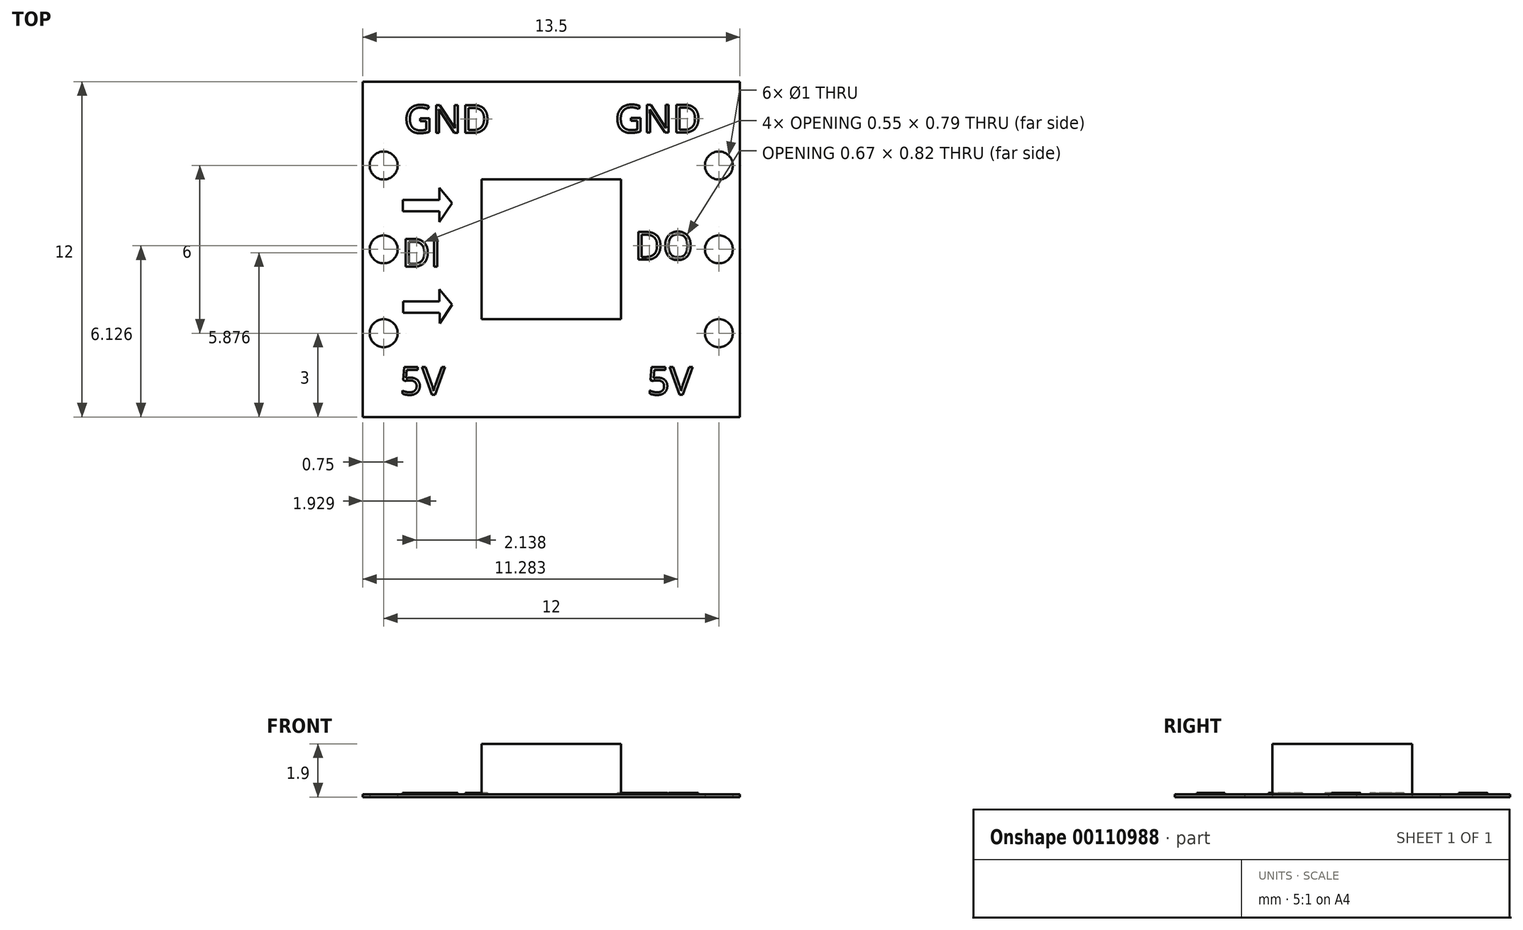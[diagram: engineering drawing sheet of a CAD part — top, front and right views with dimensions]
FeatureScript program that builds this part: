
annotation { "Feature Type Name" : "Feature", "Feature Type Description" : "" }
export const myFeature = defineFeature(function(context is Context, id is Id, definition is map)
    precondition{}
    {
        {
            var Q0;
            Q0=qCreatedBy(makeId("Top.planeOp"),FACE);
            var sketch = newSketch(context, id + "F0", { "sketchPlane" : qUnion([Q0])});
            skLineSegment(sketch, "E0.bottom", {"start": v(6.75, 6) * mm, "end": v(-6.75, 6) * mm});
            skLineSegment(sketch, "E0.top", {"start": v(6.75, -6) * mm, "end": v(-6.75, -6) * mm});
            skLineSegment(sketch, "E0.left", {"start": v(6.75, 6) * mm, "end": v(6.75, -6) * mm});
            skLineSegment(sketch, "E0.right", {"start": v(-6.75, 6) * mm, "end": v(-6.75, -6) * mm});
            skPoint(sketch, "E0.middle", {"position": v(0, 0) * mm});
            skCircle(sketch, "E1", {"center": v(-6, 3) * mm, "radius": 0.5 * mm});
            skCircle(sketch, "E2", {"center": v(6, 3) * mm, "radius": 0.5 * mm});
            skCircle(sketch, "E3.1.0.0", {"center": v(-6, 0) * mm, "radius": 0.5 * mm});
            skCircle(sketch, "E3.1.0.1", {"center": v(6, 0) * mm, "radius": 0.5 * mm});
            skCircle(sketch, "E3.2.0.0", {"center": v(-6, -3) * mm, "radius": 0.5 * mm});
            skCircle(sketch, "E3.2.0.1", {"center": v(6, -3) * mm, "radius": 0.5 * mm});
            skLineSegment(sketch, "E3.direction1", {"start": v(-6, 3) * mm, "end": v(-6, 0) * mm, "construction": true});
            skSolve(sketch);
        }
        {
            var Q0;
            Q0 = qSketchRegion(id + "F0", true);
            extrude(context, id + "F1", {"entities" : qUnion([Q0]), "depth" : 0.1 * mm});
        }
        {
            var Q0;
            Q0=makeQuery(id+"F1.opExtrude","CAP_FACE",FACE,{"disambiguationData":[OSD([sQuery(id+"F0.wireOp",EDGE,"E0.bottom"),sQuery(id+"F0.wireOp",EDGE,"E0.top"),sQuery(id+"F0.wireOp",EDGE,"E0.left"),sQuery(id+"F0.wireOp",EDGE,"E0.right"),sQuery(id+"F0.wireOp",EDGE,"E1"),sQuery(id+"F0.wireOp",EDGE,"E2"),sQuery(id+"F0.wireOp",EDGE,"E3.1.0.0"),sQuery(id+"F0.wireOp",EDGE,"E3.1.0.1"),sQuery(id+"F0.wireOp",EDGE,"E3.2.0.0"),sQuery(id+"F0.wireOp",EDGE,"E3.2.0.1")])],"isStart":false});
            var sketch = newSketch(context, id + "F2", { "sketchPlane" : qUnion([Q0])});
            skLineSegment(sketch, "E4.bottom", {"start": v(2.5, 2.5) * mm, "end": v(-2.5, 2.5) * mm});
            skLineSegment(sketch, "E4.top", {"start": v(2.5, -2.5) * mm, "end": v(-2.5, -2.5) * mm});
            skLineSegment(sketch, "E4.left", {"start": v(2.5, 2.5) * mm, "end": v(2.5, -2.5) * mm});
            skLineSegment(sketch, "E4.right", {"start": v(-2.5, 2.5) * mm, "end": v(-2.5, -2.5) * mm});
            skPoint(sketch, "E4.middle", {"position": v(0, 0) * mm});
            skSolve(sketch);
        }
        {
            var Q0;
            Q0=makeQuery(id+"F2.imprint","IMPRINT",FACE,{"disambiguationData":[TD([[makeQuery(id+"F2.imprint","IMPRINT",EDGE,{"derivedFrom":sQuery(id+"F2.wireOp",EDGE,"E4.bottom")}),1.0]])]});
            extrude(context, id + "F3", {"entities" : qUnion([Q0]), "operationType" : NewBodyOperationType.ADD, "depth" : 1.8 * mm});
        }
        {
            var Q0;
            Q0=makeQuery(id+"F1.opExtrude","CAP_FACE",FACE,{"disambiguationData":[OSD([sQuery(id+"F0.wireOp",EDGE,"E0.bottom"),sQuery(id+"F0.wireOp",EDGE,"E0.top"),sQuery(id+"F0.wireOp",EDGE,"E0.left"),sQuery(id+"F0.wireOp",EDGE,"E0.right"),sQuery(id+"F0.wireOp",EDGE,"E1"),sQuery(id+"F0.wireOp",EDGE,"E2"),sQuery(id+"F0.wireOp",EDGE,"E3.1.0.0"),sQuery(id+"F0.wireOp",EDGE,"E3.1.0.1"),sQuery(id+"F0.wireOp",EDGE,"E3.2.0.0"),sQuery(id+"F0.wireOp",EDGE,"E3.2.0.1")])],"isStart":false});
            var sketch = newSketch(context, id + "F4", { "sketchPlane" : qUnion([Q0])});
            skText(sketch, "E5", { "text": "GND", "fontName": "OpenSans-Regular.ttf"});
            skText(sketch, "E6", { "text": "DI", "fontName": "OpenSans-Regular.ttf"});
            skText(sketch, "E7", { "text": "5V", "fontName": "OpenSans-Regular.ttf"});
            skText(sketch, "E8", { "text": "GND", "fontName": "OpenSans-Regular.ttf"});
            skText(sketch, "E9", { "text": "5V", "fontName": "OpenSans-Regular.ttf"});
            skLineSegment(sketch, "E10.bottom", {"start": v(-5.32, 1.77) * mm, "end": v(-4.01, 1.77) * mm});
            skLineSegment(sketch, "E10.top", {"start": v(-5.32, 1.36) * mm, "end": v(-4.01, 1.36) * mm});
            skLineSegment(sketch, "E10.left", {"start": v(-5.32, 1.77) * mm, "end": v(-5.32, 1.36) * mm});
            skLineSegment(sketch, "E11", {"start": v(-4.01, 1.77) * mm, "end": v(-4.01, 2.2) * mm});
            skLineSegment(sketch, "E12", {"start": v(-4.01, 2.2) * mm, "end": v(-3.56, 1.65) * mm});
            skLineSegment(sketch, "E13", {"start": v(-3.56, 1.65) * mm, "end": v(-4, 0.99) * mm});
            skLineSegment(sketch, "E14", {"start": v(-4, 0.99) * mm, "end": v(-4, 1.31) * mm});
            skLineSegment(sketch, "E15", {"start": v(-4.01, 1.36) * mm, "end": v(-4, 1.31) * mm});
            skLineSegment(sketch, "E16.bottom", {"start": v(-5.3, -1.86) * mm, "end": v(-4, -1.86) * mm});
            skLineSegment(sketch, "E16.top", {"start": v(-5.3, -2.27) * mm, "end": v(-4, -2.27) * mm});
            skLineSegment(sketch, "E16.left", {"start": v(-5.3, -1.86) * mm, "end": v(-5.3, -2.27) * mm});
            skLineSegment(sketch, "E17", {"start": v(-4, -1.86) * mm, "end": v(-4, -1.43) * mm});
            skLineSegment(sketch, "E18", {"start": v(-4, -1.43) * mm, "end": v(-3.54, -1.98) * mm});
            skLineSegment(sketch, "E19", {"start": v(-3.54, -1.98) * mm, "end": v(-4, -2.64) * mm});
            skLineSegment(sketch, "E20", {"start": v(-4, -2.64) * mm, "end": v(-4, -2.32) * mm});
            skLineSegment(sketch, "E21", {"start": v(-4, -2.27) * mm, "end": v(-4, -2.32) * mm});
            skText(sketch, "E22", { "text": "DO\n", "fontName": "OpenSans-Regular.ttf"});
            const initialGuessF4  = {"E5": [-0.00527, 0.00417, 1, 0, 0.001], "E6": [-0.00535, -0.00062, 1, 0, 0.001], "E7": [-0.00542, -0.0052, 1, 0, 0.001], "E8": [0.00228, 0.00418, 1, 0, 0.001], "E9": [0.00344, -0.0052, 1, 0, 0.001], "E22": [0.00298, -0.00037, 1, 0, 0.001]};
            skSetInitialGuess(sketch, initialGuessF4);
            skSolve(sketch);
        }
        {
            var Q0;
            Q0 = qSketchRegion(id + "F4", true);
            extrude(context, id + "F5", {"entities" : qUnion([Q0]), "depth" : 0.05 * mm});
        }
    });
